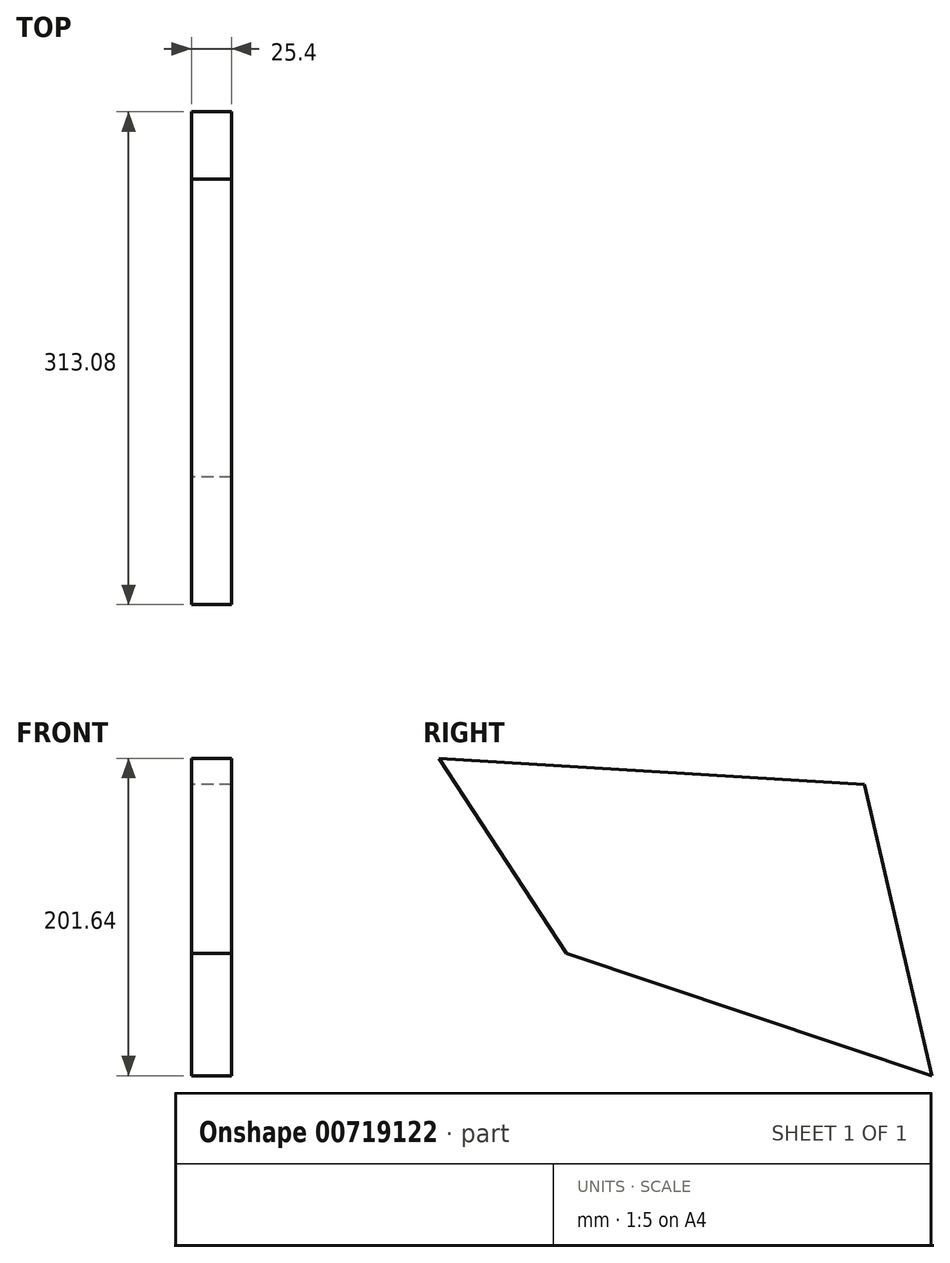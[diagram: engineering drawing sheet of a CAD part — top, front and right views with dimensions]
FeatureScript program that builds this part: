
annotation { "Feature Type Name" : "Feature", "Feature Type Description" : "" }
export const myFeature = defineFeature(function(context is Context, id is Id, definition is map)
    precondition{}
    {
        {
            var Q0;
            Q0=qCreatedBy(makeId("Right.planeOp"),FACE);
            var sketch = newSketch(context, id + "F0", { "sketchPlane" : qUnion([Q0])});
            skLineSegment(sketch, "E0", {"start": v(-96.04, 23.1) * mm, "end": v(174.16, 6.35) * mm});
            skLineSegment(sketch, "E1", {"start": v(174.16, 6.35) * mm, "end": v(217.04, -178.55) * mm});
            skLineSegment(sketch, "E2", {"start": v(217.04, -178.55) * mm, "end": v(-14.98, -100.86) * mm});
            skLineSegment(sketch, "E3", {"start": v(-14.98, -100.86) * mm, "end": v(-96.04, 23.1) * mm});
            skSolve(sketch);
        }
        {
            var Q0;
            Q0 = qSketchRegion(id + "F0", true);
            extrude(context, id + "F1", {"entities" : qUnion([Q0]), "depth" : 25.4 * mm, "offsetDistance" : 25.4 * mm});
        }
    });
